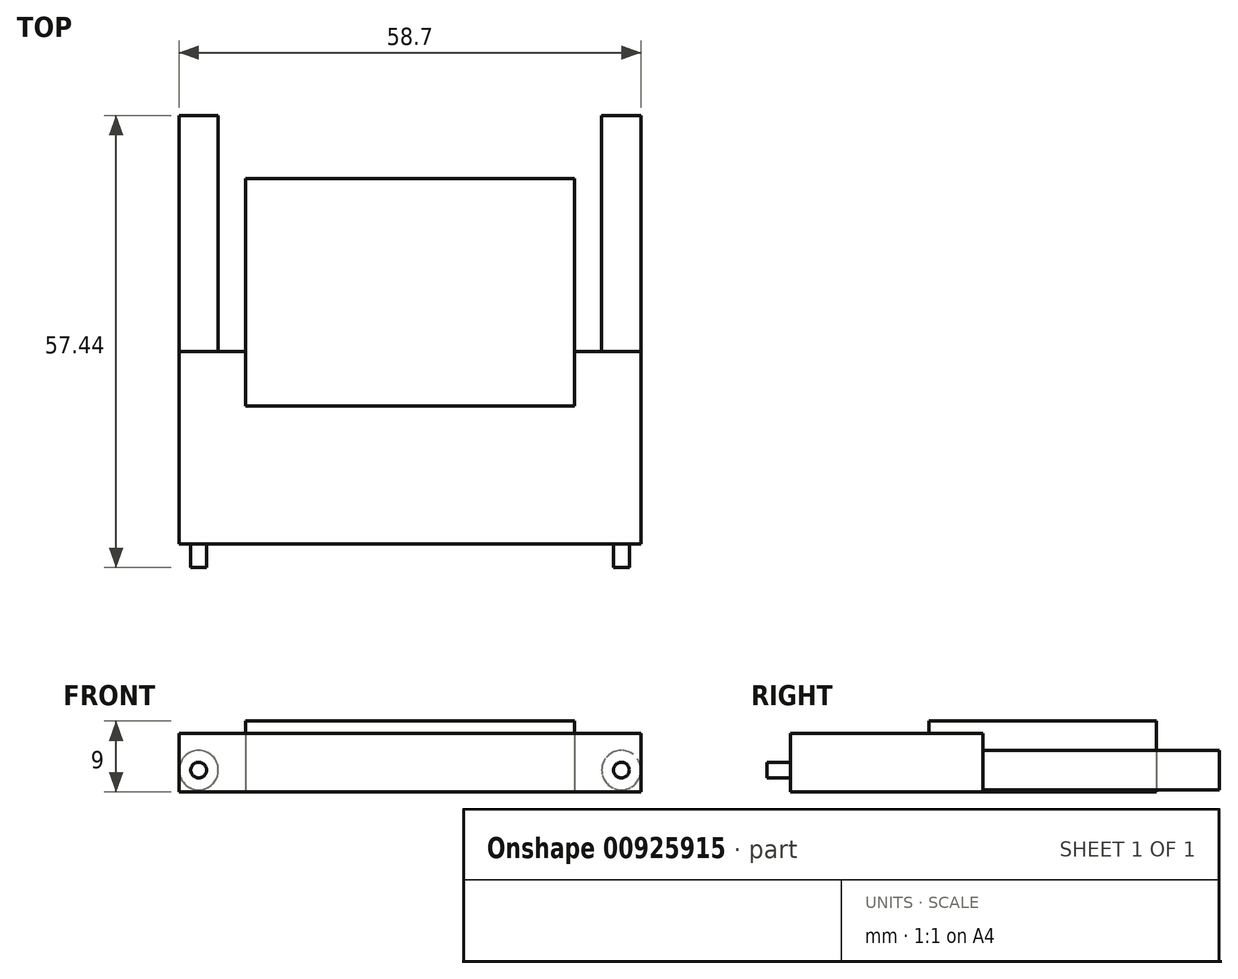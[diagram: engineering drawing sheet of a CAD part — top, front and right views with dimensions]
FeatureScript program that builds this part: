
annotation { "Feature Type Name" : "Feature", "Feature Type Description" : "" }
export const myFeature = defineFeature(function(context is Context, id is Id, definition is map)
    precondition{}
    {
        {
            var Q0;
            Q0=qCreatedBy(makeId("Top.planeOp"),FACE);
            var sketch = newSketch(context, id + "F0", { "sketchPlane" : qUnion([Q0])});
            skLineSegment(sketch, "E0.bottom", {"start": v(29.35, 0) * mm, "end": v(-29.35, 0) * mm});
            skLineSegment(sketch, "E0.top", {"start": v(29.35, 24.44) * mm, "end": v(-29.35, 24.44) * mm});
            skLineSegment(sketch, "E0.left", {"start": v(29.35, 0) * mm, "end": v(29.35, 24.44) * mm});
            skLineSegment(sketch, "E0.right", {"start": v(-29.35, 0) * mm, "end": v(-29.35, 24.44) * mm});
            skPoint(sketch, "E0.middle", {"position": v(0, 12.22) * mm});
            skLineSegment(sketch, "E1.bottom", {"start": v(20.9, 24.44) * mm, "end": v(-20.9, 24.44) * mm});
            skLineSegment(sketch, "E1.top", {"start": v(20.9, 46.44) * mm, "end": v(-20.9, 46.44) * mm});
            skLineSegment(sketch, "E1.left", {"start": v(20.9, 24.44) * mm, "end": v(20.9, 46.44) * mm});
            skLineSegment(sketch, "E1.right", {"start": v(-20.9, 24.44) * mm, "end": v(-20.9, 46.44) * mm});
            skPoint(sketch, "E1.middle", {"position": v(0, 35.44) * mm});
            skSolve(sketch);
        }
        {
            var Q0;
            Q0 = qSketchRegion(id + "F0", true);
            extrude(context, id + "F1", {"entities" : qUnion([Q0]), "depth" : 7.45 * mm, "offsetDistance" : 25 * mm});
        }
        {
            var Q0;
            Q0=makeQuery(id+"F1.opExtrude","CAP_FACE",FACE,{"disambiguationData":[OSD([sQuery(id+"F0.wireOp",EDGE,"E0.bottom"),sQuery(id+"F0.wireOp",EDGE,"E0.top"),sQuery(id+"F0.wireOp",EDGE,"E0.left"),sQuery(id+"F0.wireOp",EDGE,"E0.right"),sQuery(id+"F0.wireOp",EDGE,"E1.top"),sQuery(id+"F0.wireOp",EDGE,"E1.left"),sQuery(id+"F0.wireOp",EDGE,"E1.right")])],"isStart":false});
            var sketch = newSketch(context, id + "F2", { "sketchPlane" : qUnion([Q0])});
            skLineSegment(sketch, "E2.bottom", {"start": v(20.9, 46.44) * mm, "end": v(-20.9, 46.44) * mm});
            skLineSegment(sketch, "E2.top", {"start": v(20.9, 17.54) * mm, "end": v(-20.9, 17.54) * mm});
            skLineSegment(sketch, "E2.left", {"start": v(20.9, 46.44) * mm, "end": v(20.9, 17.54) * mm});
            skLineSegment(sketch, "E2.right", {"start": v(-20.9, 46.44) * mm, "end": v(-20.9, 17.54) * mm});
            skPoint(sketch, "E2.middle", {"position": v(0, 32) * mm});
            skSolve(sketch);
        }
        {
            var Q0;
            Q0 = qSketchRegion(id + "F2", true);
            extrude(context, id + "F3", {"entities" : qUnion([Q0]), "operationType" : NewBodyOperationType.ADD, "depth" : 1.55 * mm, "offsetDistance" : 25 * mm});
        }
        {
            var Q0;
            Q0=makeQuery(id+"F1.opExtrude","SWEPT_FACE",FACE,{"disambiguationData":[OSD([sQuery(id+"F0.wireOp",EDGE,"E0.bottom")])]});
            var sketch = newSketch(context, id + "F4", { "sketchPlane" : qUnion([Q0])});
            skCircle(sketch, "E3", {"center": v(-26.85, 2.78) * mm, "radius": 1 * mm});
            skCircle(sketch, "E4", {"center": v(26.85, 2.78) * mm, "radius": 1 * mm});
            skSolve(sketch);
        }
        {
            var Q0;
            Q0 = qSketchRegion(id + "F4", true);
            extrude(context, id + "F5", {"entities" : qUnion([Q0]), "operationType" : NewBodyOperationType.ADD, "depth" : 3 * mm, "offsetDistance" : 25 * mm});
        }
        {
            var Q0;
            {var subQ0=sQuery(id+"F0.wireOp",EDGE,"E0.top");Q0=makeQuery(id+"F1.opExtrude","SWEPT_FACE",FACE,{"disambiguationData":[OSD([subQ0]),TDD([makeQuery(id+"F0.imprint","IMPRINT",EDGE,{"disambiguationData":[TD([[makeQuery(id+"F0.imprint","INTERSECT",VERTEX,{"derivedFrom":[subQ0,sQuery(id+"F0.wireOp",EDGE,"E0.left")]}),-1.0]])],"derivedFrom":subQ0})])]});}
            var sketch = newSketch(context, id + "F6", { "sketchPlane" : qUnion([Q0])});
            skCircle(sketch, "E5", {"center": v(-26.85, 2.78) * mm, "radius": 2.5 * mm});
            skCircle(sketch, "E6", {"center": v(26.85, 2.78) * mm, "radius": 2.5 * mm});
            skSolve(sketch);
        }
        {
            var Q0;
            Q0 = qSketchRegion(id + "F6", true);
            extrude(context, id + "F7", {"entities" : qUnion([Q0]), "operationType" : NewBodyOperationType.ADD, "depth" : 30 * mm, "offsetDistance" : 25 * mm});
        }
    });
